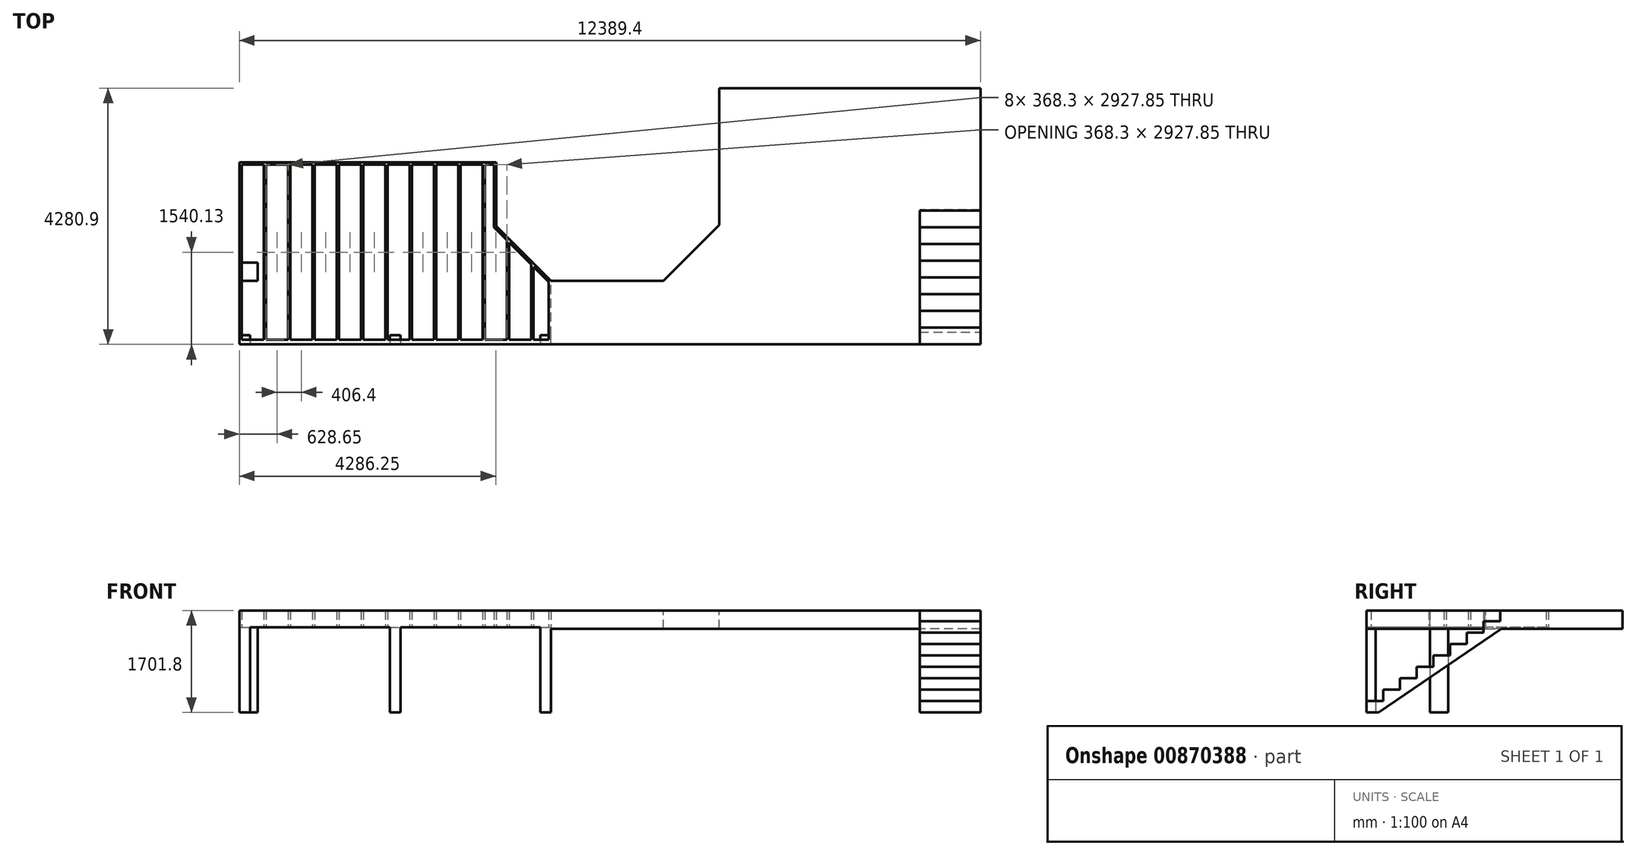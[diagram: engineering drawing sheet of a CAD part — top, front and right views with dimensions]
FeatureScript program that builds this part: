
annotation { "Feature Type Name" : "Feature", "Feature Type Description" : "" }
export const myFeature = defineFeature(function(context is Context, id is Id, definition is map)
    precondition{}
    {
        {
            var Q0;
            Q0=qCreatedBy(makeId("Top.planeOp"),FACE);
            var sketch = newSketch(context, id + "F0", { "sketchPlane" : qUnion([Q0])});
            skLineSegment(sketch, "E0.bottom", {"start": v(0, -1676.4) * mm, "end": v(304.8, -1676.4) * mm});
            skLineSegment(sketch, "E0.top", {"start": v(0, -1981.2) * mm, "end": v(304.8, -1981.2) * mm});
            skLineSegment(sketch, "E0.left", {"start": v(0, -1676.4) * mm, "end": v(0, -1981.2) * mm});
            skLineSegment(sketch, "E0.right", {"start": v(304.8, -1676.4) * mm, "end": v(304.8, -1981.2) * mm});
            skLineSegment(sketch, "E1.bottom", {"start": v(0, -2889.75) * mm, "end": v(177.8, -2889.75) * mm});
            skLineSegment(sketch, "E1.top", {"start": v(0, -3042.15) * mm, "end": v(177.8, -3042.15) * mm});
            skLineSegment(sketch, "E1.left", {"start": v(0, -2889.75) * mm, "end": v(0, -3042.15) * mm});
            skLineSegment(sketch, "E1.right", {"start": v(177.8, -2889.75) * mm, "end": v(177.8, -3042.15) * mm});
            skLineSegment(sketch, "E2.bottom", {"start": v(2514.6, -2889.75) * mm, "end": v(2692.4, -2889.75) * mm});
            skLineSegment(sketch, "E2.top", {"start": v(2514.6, -3042.15) * mm, "end": v(2692.4, -3042.15) * mm});
            skLineSegment(sketch, "E2.left", {"start": v(2514.6, -2889.75) * mm, "end": v(2514.6, -3042.15) * mm});
            skLineSegment(sketch, "E2.right", {"start": v(2692.4, -2889.75) * mm, "end": v(2692.4, -3042.15) * mm});
            skLineSegment(sketch, "E3.bottom", {"start": v(5029.2, -2889.75) * mm, "end": v(5207, -2889.75) * mm});
            skLineSegment(sketch, "E3.top", {"start": v(5029.2, -3042.15) * mm, "end": v(5207, -3042.15) * mm});
            skLineSegment(sketch, "E3.left", {"start": v(5029.2, -2889.75) * mm, "end": v(5029.2, -3042.15) * mm});
            skLineSegment(sketch, "E3.right", {"start": v(5207, -2889.75) * mm, "end": v(5207, -3042.15) * mm});
            skLineSegment(sketch, "E4", {"start": v(0, 0) * mm, "end": v(4292.6, 0) * mm, "construction": true});
            skLineSegment(sketch, "E5", {"start": v(4292.6, 0) * mm, "end": v(4292.6, -1066.8) * mm, "construction": true});
            skLineSegment(sketch, "E6", {"start": v(4292.6, -1066.8) * mm, "end": v(5226.55, -2000.75) * mm, "construction": true});
            skLineSegment(sketch, "E7", {"start": v(5226.55, -2000.75) * mm, "end": v(7106.15, -2000.75) * mm, "construction": true});
            skSolve(sketch);
        }
        {
            var Q0;
            Q0=qSketchRegion(id+"F0",true);
            extrude(context, id + "F1", {"entities" : qUnion([Q0]), "depth" : 1422.4 * mm, "offsetDistance" : 25.4 * mm});
        }
        {
            var Q0;
            Q0=makeQuery(id+"F1.opExtrude","CAP_FACE",FACE,{"disambiguationData":[OSD([sQuery(id+"F0.wireOp",EDGE,"E0.bottom"),sQuery(id+"F0.wireOp",EDGE,"E0.top"),sQuery(id+"F0.wireOp",EDGE,"E0.left"),sQuery(id+"F0.wireOp",EDGE,"E0.right")])],"isStart":false});
            var sketch = newSketch(context, id + "F2", { "sketchPlane" : qUnion([Q0])});
            skLineSegment(sketch, "E8.0", {"start": v(0, 0) * mm, "end": v(4292.6, 0) * mm});
            skLineSegment(sketch, "E9.0", {"start": v(4292.6, 0) * mm, "end": v(4292.6, -1066.8) * mm});
            skLineSegment(sketch, "E9.1", {"start": v(4292.6, -1066.8) * mm, "end": v(5207, -1981.2) * mm});
            skLineSegment(sketch, "E10", {"start": v(0, 0) * mm, "end": v(0, -3042.15) * mm});
            skLineSegment(sketch, "E11", {"start": v(0, -3042.15) * mm, "end": v(5207, -3042.15) * mm});
            skLineSegment(sketch, "E12", {"start": v(5207, -3042.15) * mm, "end": v(5207, -1981.2) * mm});
            skPoint(sketch, "E13.orphan", {"position": v(5226.55, -2000.75) * mm});
            skLineSegment(sketch, "E14.0", {"start": v(4254.5, -38.1) * mm, "end": v(4254.5, -1082.58) * mm});
            skLineSegment(sketch, "E14.1", {"start": v(5168.9, -3004.05) * mm, "end": v(5168.9, -1996.98) * mm});
            skLineSegment(sketch, "E14.2", {"start": v(38.1, -3004.05) * mm, "end": v(5168.9, -3004.05) * mm});
            skLineSegment(sketch, "E14.3", {"start": v(4254.5, -1082.58) * mm, "end": v(5168.9, -1996.98) * mm});
            skLineSegment(sketch, "E14.4", {"start": v(38.1, -38.1) * mm, "end": v(38.1, -3004.05) * mm});
            skLineSegment(sketch, "E14.5", {"start": v(38.1, -38.1) * mm, "end": v(4254.5, -38.1) * mm});
            skSolve(sketch);
        }
        {
            var Q0;
            Q0=qSketchRegion(id+"F2",true);
            extrude(context, id + "F3", {"entities" : qUnion([Q0]), "operationType" : NewBodyOperationType.ADD, "depth" : 279.4 * mm, "offsetDistance" : 25.4 * mm});
        }
        {
            var Q0;
            Q0=makeQuery(id+"F1.opExtrude","CAP_FACE",FACE,{"disambiguationData":[OSD([sQuery(id+"F0.wireOp",EDGE,"E1.bottom"),sQuery(id+"F0.wireOp",EDGE,"E1.top"),sQuery(id+"F0.wireOp",EDGE,"E1.left"),sQuery(id+"F0.wireOp",EDGE,"E1.right")])],"isStart":false});
            var sketch = newSketch(context, id + "F4", { "sketchPlane" : qUnion([Q0])});
            skPoint(sketch, "E15.oppositeSnap0", {"position": v(38.1, -2965.95) * mm});
            skLineSegment(sketch, "E15.bottom", {"start": v(38.1, -3004.05) * mm, "end": v(5168.9, -3004.05) * mm});
            skLineSegment(sketch, "E15.top", {"start": v(38.1, -2965.95) * mm, "end": v(5168.9, -2965.95) * mm});
            skLineSegment(sketch, "E15.left", {"start": v(38.1, -3004.05) * mm, "end": v(38.1, -2965.95) * mm});
            skLineSegment(sketch, "E15.right", {"start": v(5168.9, -3004.05) * mm, "end": v(5168.9, -2965.95) * mm});
            skSolve(sketch);
        }
        {
            var Q0;
            Q0=qSketchRegion(id+"F4",true);
            var Q1;
            Q1=makeQuery(id+"F3.opExtrude","CAP_FACE",FACE,{"disambiguationData":[OSD([sQuery(id+"F2.wireOp",EDGE,"E8.0"),sQuery(id+"F2.wireOp",EDGE,"E9.0"),sQuery(id+"F2.wireOp",EDGE,"E9.1"),sQuery(id+"F2.wireOp",EDGE,"E10"),sQuery(id+"F2.wireOp",EDGE,"E11"),sQuery(id+"F2.wireOp",EDGE,"E12"),sQuery(id+"F2.wireOp",EDGE,"E14.0"),sQuery(id+"F2.wireOp",EDGE,"E14.1"),sQuery(id+"F2.wireOp",EDGE,"E14.2"),sQuery(id+"F2.wireOp",EDGE,"E14.3"),sQuery(id+"F2.wireOp",EDGE,"E14.4"),sQuery(id+"F2.wireOp",EDGE,"E14.5")])],"isStart":false});
            extrude(context, id + "F5", {"entities" : qUnion([Q0]), "operationType" : NewBodyOperationType.ADD, "endBound" : BoundingType.UP_TO_SURFACE, "depth" : 25.4 * mm, "endBoundEntityFace" : qUnion([Q1]), "offsetDistance" : 25.4 * mm});
        }
        {
            var Q0;
            Q0=makeQuery(id+"F1.opExtrude","CAP_FACE",FACE,{"disambiguationData":[OSD([sQuery(id+"F0.wireOp",EDGE,"E0.bottom"),sQuery(id+"F0.wireOp",EDGE,"E0.top"),sQuery(id+"F0.wireOp",EDGE,"E0.left"),sQuery(id+"F0.wireOp",EDGE,"E0.right")])],"isStart":false});
            var sketch = newSketch(context, id + "F6", { "sketchPlane" : qUnion([Q0])});
            skLineSegment(sketch, "E16.bottom", {"start": v(406.4, -38.1) * mm, "end": v(444.5, -38.1) * mm});
            skLineSegment(sketch, "E16.top", {"start": v(406.4, -2965.95) * mm, "end": v(444.5, -2965.95) * mm});
            skLineSegment(sketch, "E16.left", {"start": v(406.4, -38.1) * mm, "end": v(406.4, -2965.95) * mm});
            skLineSegment(sketch, "E16.right", {"start": v(444.5, -38.1) * mm, "end": v(444.5, -2965.95) * mm});
            skLineSegment(sketch, "E17.1.0.0", {"start": v(850.9, -38.1) * mm, "end": v(850.9, -2965.95) * mm});
            skLineSegment(sketch, "E17.1.0.1", {"start": v(812.8, -38.1) * mm, "end": v(812.8, -2965.95) * mm});
            skLineSegment(sketch, "E17.1.0.2", {"start": v(812.8, -38.1) * mm, "end": v(850.9, -38.1) * mm});
            skLineSegment(sketch, "E17.1.0.3", {"start": v(812.8, -2965.95) * mm, "end": v(850.9, -2965.95) * mm});
            skLineSegment(sketch, "E17.2.0.0", {"start": v(1257.3, -38.1) * mm, "end": v(1257.3, -2965.95) * mm});
            skLineSegment(sketch, "E17.2.0.1", {"start": v(1219.2, -38.1) * mm, "end": v(1219.2, -2965.95) * mm});
            skLineSegment(sketch, "E17.2.0.2", {"start": v(1219.2, -38.1) * mm, "end": v(1257.3, -38.1) * mm});
            skLineSegment(sketch, "E17.2.0.3", {"start": v(1219.2, -2965.95) * mm, "end": v(1257.3, -2965.95) * mm});
            skLineSegment(sketch, "E17.3.0.0", {"start": v(1663.7, -38.1) * mm, "end": v(1663.7, -2965.95) * mm});
            skLineSegment(sketch, "E17.3.0.1", {"start": v(1625.6, -38.1) * mm, "end": v(1625.6, -2965.95) * mm});
            skLineSegment(sketch, "E17.3.0.2", {"start": v(1625.6, -38.1) * mm, "end": v(1663.7, -38.1) * mm});
            skLineSegment(sketch, "E17.3.0.3", {"start": v(1625.6, -2965.95) * mm, "end": v(1663.7, -2965.95) * mm});
            skLineSegment(sketch, "E17.4.0.0", {"start": v(2070.1, -38.1) * mm, "end": v(2070.1, -2965.95) * mm});
            skLineSegment(sketch, "E17.4.0.1", {"start": v(2032, -38.1) * mm, "end": v(2032, -2965.95) * mm});
            skLineSegment(sketch, "E17.4.0.2", {"start": v(2032, -38.1) * mm, "end": v(2070.1, -38.1) * mm});
            skLineSegment(sketch, "E17.4.0.3", {"start": v(2032, -2965.95) * mm, "end": v(2070.1, -2965.95) * mm});
            skLineSegment(sketch, "E17.5.0.0", {"start": v(2476.5, -38.1) * mm, "end": v(2476.5, -2965.95) * mm});
            skLineSegment(sketch, "E17.5.0.1", {"start": v(2438.4, -38.1) * mm, "end": v(2438.4, -2965.95) * mm});
            skLineSegment(sketch, "E17.5.0.2", {"start": v(2438.4, -38.1) * mm, "end": v(2476.5, -38.1) * mm});
            skLineSegment(sketch, "E17.5.0.3", {"start": v(2438.4, -2965.95) * mm, "end": v(2476.5, -2965.95) * mm});
            skLineSegment(sketch, "E17.6.0.0", {"start": v(2882.9, -38.1) * mm, "end": v(2882.9, -2965.95) * mm});
            skLineSegment(sketch, "E17.6.0.1", {"start": v(2844.8, -38.1) * mm, "end": v(2844.8, -2965.95) * mm});
            skLineSegment(sketch, "E17.6.0.2", {"start": v(2844.8, -38.1) * mm, "end": v(2882.9, -38.1) * mm});
            skLineSegment(sketch, "E17.6.0.3", {"start": v(2844.8, -2965.95) * mm, "end": v(2882.9, -2965.95) * mm});
            skLineSegment(sketch, "E17.7.0.0", {"start": v(3289.3, -38.1) * mm, "end": v(3289.3, -2965.95) * mm});
            skLineSegment(sketch, "E17.7.0.1", {"start": v(3251.2, -38.1) * mm, "end": v(3251.2, -2965.95) * mm});
            skLineSegment(sketch, "E17.7.0.2", {"start": v(3251.2, -38.1) * mm, "end": v(3289.3, -38.1) * mm});
            skLineSegment(sketch, "E17.7.0.3", {"start": v(3251.2, -2965.95) * mm, "end": v(3289.3, -2965.95) * mm});
            skLineSegment(sketch, "E17.8.0.0", {"start": v(3695.7, -38.1) * mm, "end": v(3695.7, -2965.95) * mm});
            skLineSegment(sketch, "E17.8.0.1", {"start": v(3657.6, -38.1) * mm, "end": v(3657.6, -2965.95) * mm});
            skLineSegment(sketch, "E17.8.0.2", {"start": v(3657.6, -38.1) * mm, "end": v(3695.7, -38.1) * mm});
            skLineSegment(sketch, "E17.8.0.3", {"start": v(3657.6, -2965.95) * mm, "end": v(3695.7, -2965.95) * mm});
            skLineSegment(sketch, "E17.9.0.0", {"start": v(4102.1, -38.1) * mm, "end": v(4102.1, -2965.95) * mm});
            skLineSegment(sketch, "E17.9.0.1", {"start": v(4064, -38.1) * mm, "end": v(4064, -2965.95) * mm});
            skLineSegment(sketch, "E17.9.0.2", {"start": v(4064, -38.1) * mm, "end": v(4102.1, -38.1) * mm});
            skLineSegment(sketch, "E17.9.0.3", {"start": v(4064, -2965.95) * mm, "end": v(4102.1, -2965.95) * mm});
            skLineSegment(sketch, "E17.direction1", {"start": v(406.4, -2965.95) * mm, "end": v(812.8, -2965.95) * mm, "construction": true});
            skLineSegment(sketch, "E18.top", {"start": v(4470.4, -2965.95) * mm, "end": v(4508.5, -2965.95) * mm});
            skLineSegment(sketch, "E18.left", {"start": v(4470.4, -1298.48) * mm, "end": v(4470.4, -2965.95) * mm});
            skLineSegment(sketch, "E18.right", {"start": v(4508.5, -1336.58) * mm, "end": v(4508.5, -2965.95) * mm});
            skLineSegment(sketch, "E19.top", {"start": v(4876.8, -2965.95) * mm, "end": v(4914.9, -2965.95) * mm});
            skLineSegment(sketch, "E19.left", {"start": v(4876.8, -1704.88) * mm, "end": v(4876.8, -2965.95) * mm});
            skLineSegment(sketch, "E19.right", {"start": v(4914.9, -1742.98) * mm, "end": v(4914.9, -2965.95) * mm});
            skLineSegment(sketch, "E20", {"start": v(4470.4, -1298.48) * mm, "end": v(4508.5, -1336.58) * mm});
            skLineSegment(sketch, "E21.trimOffspring", {"start": v(4876.8, -1704.88) * mm, "end": v(4914.9, -1742.98) * mm});
            skSolve(sketch);
        }
        {
            var Q0;
            Q0=qSketchRegion(id+"F6",true);
            var Q1;
            {var subQ0=sQuery(id+"F2.wireOp",EDGE,"E14.5");var subQ1=sQuery(id+"F2.wireOp",EDGE,"E14.4");var subQ2=sQuery(id+"F2.wireOp",EDGE,"E14.3");var subQ3=sQuery(id+"F2.wireOp",EDGE,"E14.2");var subQ4=sQuery(id+"F2.wireOp",EDGE,"E14.1");var subQ5=sQuery(id+"F2.wireOp",EDGE,"E14.0");var subQ6=sQuery(id+"F2.wireOp",EDGE,"E12");var subQ7=sQuery(id+"F2.wireOp",EDGE,"E11");var subQ8=sQuery(id+"F2.wireOp",EDGE,"E10");var subQ9=sQuery(id+"F2.wireOp",EDGE,"E9.1");var subQ10=sQuery(id+"F2.wireOp",EDGE,"E9.0");var subQ11=sQuery(id+"F2.wireOp",EDGE,"E8.0");Q1=makeQuery(id+"F5.boolean.opBoolean","MERGE",FACE,{"derivedFrom":[makeQuery(id+"F3.opExtrude","CAP_FACE",FACE,{"disambiguationData":[OSD([subQ11,subQ10,subQ9,subQ8,subQ7,subQ6,subQ5,subQ4,subQ3,subQ2,subQ1,subQ0])],"isStart":false}),makeQuery(id+"F5.opExtrude","CAP_FACE",FACE,{"disambiguationData":[OSD([subQ11,subQ10,subQ9,subQ8,subQ7,subQ6,subQ5,subQ4,subQ3,subQ2,subQ1,subQ0])],"isStart":false})]});}
            extrude(context, id + "F7", {"entities" : qUnion([Q0]), "operationType" : NewBodyOperationType.ADD, "endBound" : BoundingType.UP_TO_SURFACE, "depth" : 25.4 * mm, "endBoundEntityFace" : qUnion([Q1]), "offsetDistance" : 25.4 * mm});
        }
        {
            var Q0;
            Q0=makeQuery(id+"F7.boolean.opBoolean","MERGE",FACE,{"derivedFrom":[makeQuery(id+"F5.boolean.opBoolean","MERGE",FACE,{"derivedFrom":[makeQuery(id+"F3.opExtrude","CAP_FACE",FACE,{"disambiguationData":[OSD([sQuery(id+"F2.wireOp",EDGE,"E8.0"),sQuery(id+"F2.wireOp",EDGE,"E9.0"),sQuery(id+"F2.wireOp",EDGE,"E9.1"),sQuery(id+"F2.wireOp",EDGE,"E10"),sQuery(id+"F2.wireOp",EDGE,"E11"),sQuery(id+"F2.wireOp",EDGE,"E12"),sQuery(id+"F2.wireOp",EDGE,"E14.0"),sQuery(id+"F2.wireOp",EDGE,"E14.1"),sQuery(id+"F2.wireOp",EDGE,"E14.2"),sQuery(id+"F2.wireOp",EDGE,"E14.3"),sQuery(id+"F2.wireOp",EDGE,"E14.4"),sQuery(id+"F2.wireOp",EDGE,"E14.5")])],"isStart":false}),makeQuery(id+"F5.opExtrude","CAP_FACE",FACE,{"disambiguationData":[OSD([sQuery(id+"F4.wireOp",EDGE,"E15.bottom"),sQuery(id+"F4.wireOp",EDGE,"E15.top"),sQuery(id+"F4.wireOp",EDGE,"E15.left"),sQuery(id+"F4.wireOp",EDGE,"E15.right")])],"isStart":false})]}),makeQuery(id+"F7.opExtrude","CAP_FACE",FACE,{"disambiguationData":[OSD([sQuery(id+"F6.wireOp",EDGE,"E16.bottom"),sQuery(id+"F6.wireOp",EDGE,"E16.top"),sQuery(id+"F6.wireOp",EDGE,"E16.left"),sQuery(id+"F6.wireOp",EDGE,"E16.right")])],"isStart":false}),makeQuery(id+"F7.opExtrude","CAP_FACE",FACE,{"disambiguationData":[OSD([sQuery(id+"F6.wireOp",EDGE,"E17.1.0.0"),sQuery(id+"F6.wireOp",EDGE,"E17.1.0.1"),sQuery(id+"F6.wireOp",EDGE,"E17.1.0.2"),sQuery(id+"F6.wireOp",EDGE,"E17.1.0.3")])],"isStart":false}),makeQuery(id+"F7.opExtrude","CAP_FACE",FACE,{"disambiguationData":[OSD([sQuery(id+"F6.wireOp",EDGE,"E17.2.0.0"),sQuery(id+"F6.wireOp",EDGE,"E17.2.0.1"),sQuery(id+"F6.wireOp",EDGE,"E17.2.0.2"),sQuery(id+"F6.wireOp",EDGE,"E17.2.0.3")])],"isStart":false}),makeQuery(id+"F7.opExtrude","CAP_FACE",FACE,{"disambiguationData":[OSD([sQuery(id+"F6.wireOp",EDGE,"E17.3.0.0"),sQuery(id+"F6.wireOp",EDGE,"E17.3.0.1"),sQuery(id+"F6.wireOp",EDGE,"E17.3.0.2"),sQuery(id+"F6.wireOp",EDGE,"E17.3.0.3")])],"isStart":false}),makeQuery(id+"F7.opExtrude","CAP_FACE",FACE,{"disambiguationData":[OSD([sQuery(id+"F6.wireOp",EDGE,"E17.4.0.0"),sQuery(id+"F6.wireOp",EDGE,"E17.4.0.1"),sQuery(id+"F6.wireOp",EDGE,"E17.4.0.2"),sQuery(id+"F6.wireOp",EDGE,"E17.4.0.3")])],"isStart":false}),makeQuery(id+"F7.opExtrude","CAP_FACE",FACE,{"disambiguationData":[OSD([sQuery(id+"F6.wireOp",EDGE,"E17.5.0.0"),sQuery(id+"F6.wireOp",EDGE,"E17.5.0.1"),sQuery(id+"F6.wireOp",EDGE,"E17.5.0.2"),sQuery(id+"F6.wireOp",EDGE,"E17.5.0.3")])],"isStart":false}),makeQuery(id+"F7.opExtrude","CAP_FACE",FACE,{"disambiguationData":[OSD([sQuery(id+"F6.wireOp",EDGE,"E17.6.0.0"),sQuery(id+"F6.wireOp",EDGE,"E17.6.0.1"),sQuery(id+"F6.wireOp",EDGE,"E17.6.0.2"),sQuery(id+"F6.wireOp",EDGE,"E17.6.0.3")])],"isStart":false}),makeQuery(id+"F7.opExtrude","CAP_FACE",FACE,{"disambiguationData":[OSD([sQuery(id+"F6.wireOp",EDGE,"E17.7.0.0"),sQuery(id+"F6.wireOp",EDGE,"E17.7.0.1"),sQuery(id+"F6.wireOp",EDGE,"E17.7.0.2"),sQuery(id+"F6.wireOp",EDGE,"E17.7.0.3")])],"isStart":false}),makeQuery(id+"F7.opExtrude","CAP_FACE",FACE,{"disambiguationData":[OSD([sQuery(id+"F6.wireOp",EDGE,"E17.8.0.0"),sQuery(id+"F6.wireOp",EDGE,"E17.8.0.1"),sQuery(id+"F6.wireOp",EDGE,"E17.8.0.2"),sQuery(id+"F6.wireOp",EDGE,"E17.8.0.3")])],"isStart":false}),makeQuery(id+"F7.opExtrude","CAP_FACE",FACE,{"disambiguationData":[OSD([sQuery(id+"F6.wireOp",EDGE,"E17.9.0.0"),sQuery(id+"F6.wireOp",EDGE,"E17.9.0.1"),sQuery(id+"F6.wireOp",EDGE,"E17.9.0.2"),sQuery(id+"F6.wireOp",EDGE,"E17.9.0.3")])],"isStart":false}),makeQuery(id+"F7.opExtrude","CAP_FACE",FACE,{"disambiguationData":[OSD([sQuery(id+"F6.wireOp",EDGE,"E18.top"),sQuery(id+"F6.wireOp",EDGE,"E18.left"),sQuery(id+"F6.wireOp",EDGE,"E18.right"),sQuery(id+"F6.wireOp",EDGE,"E20")])],"isStart":false}),makeQuery(id+"F7.opExtrude","CAP_FACE",FACE,{"disambiguationData":[OSD([sQuery(id+"F6.wireOp",EDGE,"E19.top"),sQuery(id+"F6.wireOp",EDGE,"E19.left"),sQuery(id+"F6.wireOp",EDGE,"E19.right"),sQuery(id+"F6.wireOp",EDGE,"E21.trimOffspring")])],"isStart":false})]});
            var sketch = newSketch(context, id + "F8", { "sketchPlane" : qUnion([Q0])});
            skLineSegment(sketch, "E22", {"start": v(5207, -1981.2) * mm, "end": v(5207, -3042.15) * mm});
            skLineSegment(sketch, "E23", {"start": v(5207, -1981.2) * mm, "end": v(7086.6, -1981.2) * mm});
            skLineSegment(sketch, "E24", {"start": v(7086.6, -1981.2) * mm, "end": v(8020.55, -1047.25) * mm});
            skLineSegment(sketch, "E25", {"start": v(8020.55, -1047.25) * mm, "end": v(8020.55, 1238.75) * mm});
            skLineSegment(sketch, "E26", {"start": v(8020.55, 1238.75) * mm, "end": v(12389.35, 1238.75) * mm});
            skLineSegment(sketch, "E27", {"start": v(12389.35, 1238.75) * mm, "end": v(12389.35, -3042.15) * mm});
            skLineSegment(sketch, "E28", {"start": v(5207, -3042.15) * mm, "end": v(12389.35, -3042.15) * mm});
            skSolve(sketch);
        }
        {
            var Q0;
            Q0=qSketchRegion(id+"F8",true);
            extrude(context, id + "F9", {"entities" : qUnion([Q0]), "operationType" : NewBodyOperationType.ADD, "oppositeDirection" : true, "depth" : 304.8 * mm, "offsetDistance" : 25.4 * mm});
        }
        {
            var Q0;
            Q0=makeQuery(id+"F9.boolean.opBoolean","MERGE",FACE,{"derivedFrom":[makeQuery(id+"F7.boolean.opBoolean","MERGE",FACE,{"derivedFrom":[makeQuery(id+"F5.boolean.opBoolean","MERGE",FACE,{"derivedFrom":[makeQuery(id+"F3.opExtrude","CAP_FACE",FACE,{"disambiguationData":[OSD([sQuery(id+"F2.wireOp",EDGE,"E8.0"),sQuery(id+"F2.wireOp",EDGE,"E9.0"),sQuery(id+"F2.wireOp",EDGE,"E9.1"),sQuery(id+"F2.wireOp",EDGE,"E10"),sQuery(id+"F2.wireOp",EDGE,"E11"),sQuery(id+"F2.wireOp",EDGE,"E12"),sQuery(id+"F2.wireOp",EDGE,"E14.0"),sQuery(id+"F2.wireOp",EDGE,"E14.1"),sQuery(id+"F2.wireOp",EDGE,"E14.2"),sQuery(id+"F2.wireOp",EDGE,"E14.3"),sQuery(id+"F2.wireOp",EDGE,"E14.4"),sQuery(id+"F2.wireOp",EDGE,"E14.5")])],"isStart":false}),makeQuery(id+"F5.opExtrude","CAP_FACE",FACE,{"disambiguationData":[OSD([sQuery(id+"F4.wireOp",EDGE,"E15.bottom"),sQuery(id+"F4.wireOp",EDGE,"E15.top"),sQuery(id+"F4.wireOp",EDGE,"E15.left"),sQuery(id+"F4.wireOp",EDGE,"E15.right")])],"isStart":false})]}),makeQuery(id+"F7.opExtrude","CAP_FACE",FACE,{"disambiguationData":[OSD([sQuery(id+"F6.wireOp",EDGE,"E16.bottom"),sQuery(id+"F6.wireOp",EDGE,"E16.top"),sQuery(id+"F6.wireOp",EDGE,"E16.left"),sQuery(id+"F6.wireOp",EDGE,"E16.right")])],"isStart":false}),makeQuery(id+"F7.opExtrude","CAP_FACE",FACE,{"disambiguationData":[OSD([sQuery(id+"F6.wireOp",EDGE,"E17.1.0.0"),sQuery(id+"F6.wireOp",EDGE,"E17.1.0.1"),sQuery(id+"F6.wireOp",EDGE,"E17.1.0.2"),sQuery(id+"F6.wireOp",EDGE,"E17.1.0.3")])],"isStart":false}),makeQuery(id+"F7.opExtrude","CAP_FACE",FACE,{"disambiguationData":[OSD([sQuery(id+"F6.wireOp",EDGE,"E17.2.0.0"),sQuery(id+"F6.wireOp",EDGE,"E17.2.0.1"),sQuery(id+"F6.wireOp",EDGE,"E17.2.0.2"),sQuery(id+"F6.wireOp",EDGE,"E17.2.0.3")])],"isStart":false}),makeQuery(id+"F7.opExtrude","CAP_FACE",FACE,{"disambiguationData":[OSD([sQuery(id+"F6.wireOp",EDGE,"E17.3.0.0"),sQuery(id+"F6.wireOp",EDGE,"E17.3.0.1"),sQuery(id+"F6.wireOp",EDGE,"E17.3.0.2"),sQuery(id+"F6.wireOp",EDGE,"E17.3.0.3")])],"isStart":false}),makeQuery(id+"F7.opExtrude","CAP_FACE",FACE,{"disambiguationData":[OSD([sQuery(id+"F6.wireOp",EDGE,"E17.4.0.0"),sQuery(id+"F6.wireOp",EDGE,"E17.4.0.1"),sQuery(id+"F6.wireOp",EDGE,"E17.4.0.2"),sQuery(id+"F6.wireOp",EDGE,"E17.4.0.3")])],"isStart":false}),makeQuery(id+"F7.opExtrude","CAP_FACE",FACE,{"disambiguationData":[OSD([sQuery(id+"F6.wireOp",EDGE,"E17.5.0.0"),sQuery(id+"F6.wireOp",EDGE,"E17.5.0.1"),sQuery(id+"F6.wireOp",EDGE,"E17.5.0.2"),sQuery(id+"F6.wireOp",EDGE,"E17.5.0.3")])],"isStart":false}),makeQuery(id+"F7.opExtrude","CAP_FACE",FACE,{"disambiguationData":[OSD([sQuery(id+"F6.wireOp",EDGE,"E17.6.0.0"),sQuery(id+"F6.wireOp",EDGE,"E17.6.0.1"),sQuery(id+"F6.wireOp",EDGE,"E17.6.0.2"),sQuery(id+"F6.wireOp",EDGE,"E17.6.0.3")])],"isStart":false}),makeQuery(id+"F7.opExtrude","CAP_FACE",FACE,{"disambiguationData":[OSD([sQuery(id+"F6.wireOp",EDGE,"E17.7.0.0"),sQuery(id+"F6.wireOp",EDGE,"E17.7.0.1"),sQuery(id+"F6.wireOp",EDGE,"E17.7.0.2"),sQuery(id+"F6.wireOp",EDGE,"E17.7.0.3")])],"isStart":false}),makeQuery(id+"F7.opExtrude","CAP_FACE",FACE,{"disambiguationData":[OSD([sQuery(id+"F6.wireOp",EDGE,"E17.8.0.0"),sQuery(id+"F6.wireOp",EDGE,"E17.8.0.1"),sQuery(id+"F6.wireOp",EDGE,"E17.8.0.2"),sQuery(id+"F6.wireOp",EDGE,"E17.8.0.3")])],"isStart":false}),makeQuery(id+"F7.opExtrude","CAP_FACE",FACE,{"disambiguationData":[OSD([sQuery(id+"F6.wireOp",EDGE,"E17.9.0.0"),sQuery(id+"F6.wireOp",EDGE,"E17.9.0.1"),sQuery(id+"F6.wireOp",EDGE,"E17.9.0.2"),sQuery(id+"F6.wireOp",EDGE,"E17.9.0.3")])],"isStart":false}),makeQuery(id+"F7.opExtrude","CAP_FACE",FACE,{"disambiguationData":[OSD([sQuery(id+"F6.wireOp",EDGE,"E18.top"),sQuery(id+"F6.wireOp",EDGE,"E18.left"),sQuery(id+"F6.wireOp",EDGE,"E18.right"),sQuery(id+"F6.wireOp",EDGE,"E20")])],"isStart":false}),makeQuery(id+"F7.opExtrude","CAP_FACE",FACE,{"disambiguationData":[OSD([sQuery(id+"F6.wireOp",EDGE,"E19.top"),sQuery(id+"F6.wireOp",EDGE,"E19.left"),sQuery(id+"F6.wireOp",EDGE,"E19.right"),sQuery(id+"F6.wireOp",EDGE,"E21.trimOffspring")])],"isStart":false})]}),makeQuery(id+"F9.opExtrude","CAP_FACE",FACE,{"disambiguationData":[OSD([sQuery(id+"F8.wireOp",EDGE,"E22"),sQuery(id+"F8.wireOp",EDGE,"E23"),sQuery(id+"F8.wireOp",EDGE,"E24"),sQuery(id+"F8.wireOp",EDGE,"E25"),sQuery(id+"F8.wireOp",EDGE,"E26"),sQuery(id+"F8.wireOp",EDGE,"E27"),sQuery(id+"F8.wireOp",EDGE,"E28")])],"isStart":true})]});
            var sketch = newSketch(context, id + "F10", { "sketchPlane" : qUnion([Q0])});
            skLineSegment(sketch, "E29.bottom", {"start": v(12389.35, -3042.15) * mm, "end": v(11373.35, -3042.15) * mm});
            skLineSegment(sketch, "E29.top", {"start": v(12389.35, -806.95) * mm, "end": v(11373.35, -806.95) * mm});
            skLineSegment(sketch, "E29.left", {"start": v(12389.35, -3042.15) * mm, "end": v(12389.35, -806.95) * mm});
            skLineSegment(sketch, "E29.right", {"start": v(11373.35, -3042.15) * mm, "end": v(11373.35, -806.95) * mm});
            skSolve(sketch);
        }
        {
            var Q0;
            Q0 = qSketchRegion(id + "F10", true);
            extrude(context, id + "F11", {"entities" : qUnion([Q0]), "operationType" : NewBodyOperationType.REMOVE, "endBound" : BoundingType.UP_TO_NEXT, "oppositeDirection" : true, "depth" : 25.4 * mm, "offsetDistance" : 25.4 * mm});
        }
        {
            var Q0;
            Q0=makeQuery(id+"F9.opExtrude","SWEPT_FACE",FACE,{"disambiguationData":[OSD([sQuery(id+"F8.wireOp",EDGE,"E27")])]});
            var sketch = newSketch(context, id + "F12", { "sketchPlane" : qUnion([Q0])});
            skLineSegment(sketch, "E30", {"start": v(-806.95, 1701.8) * mm, "end": v(-806.95, 1524) * mm});
            skLineSegment(sketch, "E31", {"start": v(-806.95, 1524) * mm, "end": v(-1086.35, 1524) * mm});
            skLineSegment(sketch, "E32", {"start": v(-1086.35, 1524) * mm, "end": v(-1086.35, 1333.5) * mm});
            skLineSegment(sketch, "E33", {"start": v(-1086.35, 1333.5) * mm, "end": v(-1365.75, 1333.5) * mm});
            skLineSegment(sketch, "E34", {"start": v(-1365.75, 1333.5) * mm, "end": v(-1365.75, 1143) * mm});
            skLineSegment(sketch, "E35", {"start": v(-1365.75, 1143) * mm, "end": v(-1645.15, 1143) * mm});
            skLineSegment(sketch, "E36", {"start": v(-1645.15, 1143) * mm, "end": v(-1645.15, 952.5) * mm});
            skLineSegment(sketch, "E37", {"start": v(-1645.15, 952.5) * mm, "end": v(-1924.55, 952.5) * mm});
            skLineSegment(sketch, "E38", {"start": v(-1924.55, 952.5) * mm, "end": v(-1924.55, 762) * mm});
            skLineSegment(sketch, "E39", {"start": v(-1924.55, 762) * mm, "end": v(-2203.95, 762) * mm});
            skLineSegment(sketch, "E40", {"start": v(-2203.95, 762) * mm, "end": v(-2203.95, 571.5) * mm});
            skLineSegment(sketch, "E41", {"start": v(-2203.95, 571.5) * mm, "end": v(-2483.35, 571.5) * mm});
            skLineSegment(sketch, "E42", {"start": v(-2483.35, 571.5) * mm, "end": v(-2483.35, 381) * mm});
            skLineSegment(sketch, "E43", {"start": v(-2483.35, 381) * mm, "end": v(-2762.75, 381) * mm});
            skLineSegment(sketch, "E44", {"start": v(-2762.75, 381) * mm, "end": v(-2762.75, 190.5) * mm});
            skLineSegment(sketch, "E45", {"start": v(-2838.77, 0) * mm, "end": v(-342.8, 1701.8) * mm});
            skLineSegment(sketch, "E46", {"start": v(-342.8, 1701.8) * mm, "end": v(-806.95, 1701.8) * mm});
            skLineSegment(sketch, "E47", {"start": v(-2762.75, 190.5) * mm, "end": v(-3042.15, 190.5) * mm});
            skLineSegment(sketch, "E48", {"start": v(-3042.15, 190.5) * mm, "end": v(-3042.15, 0) * mm});
            skLineSegment(sketch, "E49", {"start": v(-3042.15, 0) * mm, "end": v(-2838.77, 0) * mm});
            skLineSegment(sketch, "E50", {"start": v(-3042.15, 190.5) * mm, "end": v(-1086.35, 1524) * mm, "construction": true});
            skSolve(sketch);
        }
        {
            var Q0;
            Q0 = qSketchRegion(id + "F12", true);
            var Q1;
            Q1=makeQuery(id+"F11.boolean.opBoolean","COPY",FACE,{"derivedFrom":makeQuery(id+"F11.opExtrude","SWEPT_FACE",FACE,{"disambiguationData":[OSD([sQuery(id+"F10.wireOp",EDGE,"E29.right")])]})});
            extrude(context, id + "F13", {"entities" : qUnion([Q0]), "operationType" : NewBodyOperationType.ADD, "endBound" : BoundingType.UP_TO_SURFACE, "oppositeDirection" : true, "depth" : 25.4 * mm, "endBoundEntityFace" : qUnion([Q1]), "offsetDistance" : 25.4 * mm});
        }
    });
